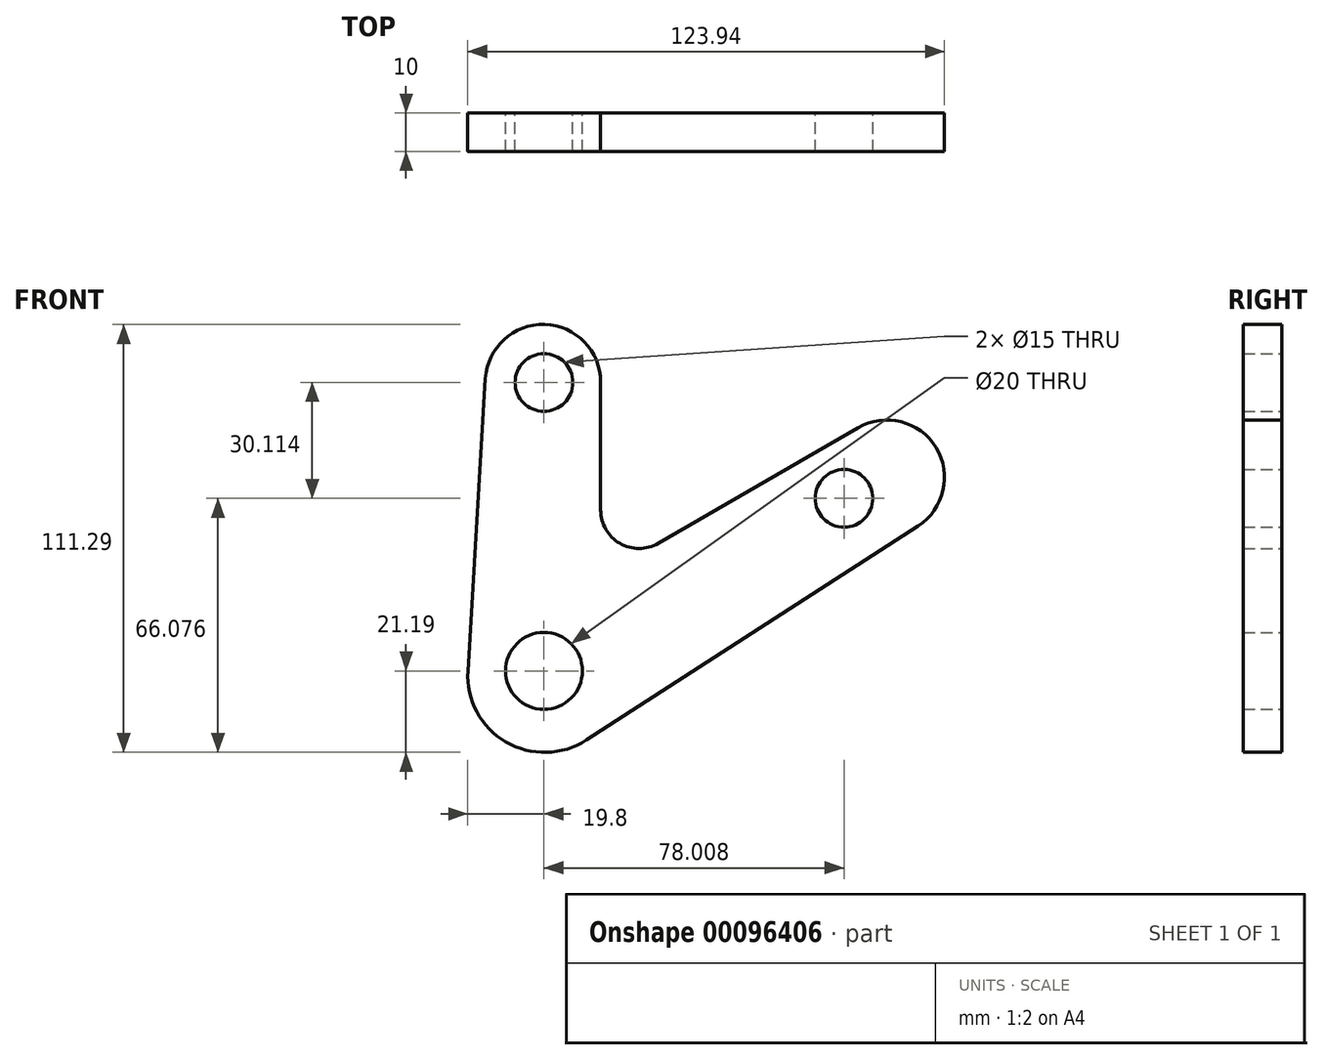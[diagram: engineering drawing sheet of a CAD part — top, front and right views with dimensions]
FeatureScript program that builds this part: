
annotation { "Feature Type Name" : "Feature", "Feature Type Description" : "" }
export const myFeature = defineFeature(function(context is Context, id is Id, definition is map)
    precondition{}
    {
        {
            var Q0;
            Q0=qCreatedBy(makeId("Front.planeOp"),FACE);
            var sketch = newSketch(context, id + "F0", { "sketchPlane" : qUnion([Q0])});
            skCircle(sketch, "E0", {"center": v(0, 0) * mm, "radius": 10 * mm});
            skCircle(sketch, "E1", {"center": v(0, 75) * mm, "radius": 7.5 * mm});
            skCircle(sketch, "E2", {"center": v(78, 44.89) * mm, "radius": 7.5 * mm});
            skArc(sketch, "E3", {"start": v(-19.76, 0) * mm, "mid": v(-9.89, -18.46) * mm, "end": v(11.05, -18) * mm});
            skLineSegment(sketch, "E4", {"start": v(11.05, -18) * mm, "end": v(97.28, 37.66) * mm});
            skLineSegment(sketch, "E5", {"start": v(-19.76, 0) * mm, "end": v(-15.23, 76) * mm});
            skLineSegment(sketch, "E6", {"start": v(14.74, 75.1) * mm, "end": v(14.74, 41.85) * mm});
            skLineSegment(sketch, "E7", {"start": v(81.62, 63.24) * mm, "end": v(29.75, 33.2) * mm});
            skPoint(sketch, "E8.visualSharp", {"position": v(14.74, 24.5) * mm});
            skArc(sketch, "E8.filletArc", {"start": v(14.74, 41.85) * mm, "mid": v(19.75, 33.18) * mm, "end": v(29.75, 33.2) * mm});
            skLineSegment(sketch, "E9", {"start": v(0, 0) * mm, "end": v(101.58, 58.65) * mm, "construction": true});
            skLineSegment(sketch, "E10", {"start": v(0, 0) * mm, "end": v(0, 82.5) * mm, "construction": true});
            skArc(sketch, "E11", {"start": v(97.28, 37.66) * mm, "mid": v(101.94, 58.1) * mm, "end": v(81.62, 63.24) * mm});
            skArc(sketch, "E12", {"start": v(14.74, 75.1) * mm, "mid": v(0.19, 90.1) * mm, "end": v(-15.23, 76) * mm});
            skSolve(sketch);
        }
        {
            var Q0;
            Q0 = qSketchRegion(id + "F0", true);
            extrude(context, id + "F1", {"entities" : qUnion([Q0]), "depth" : 10 * mm});
        }
    });
